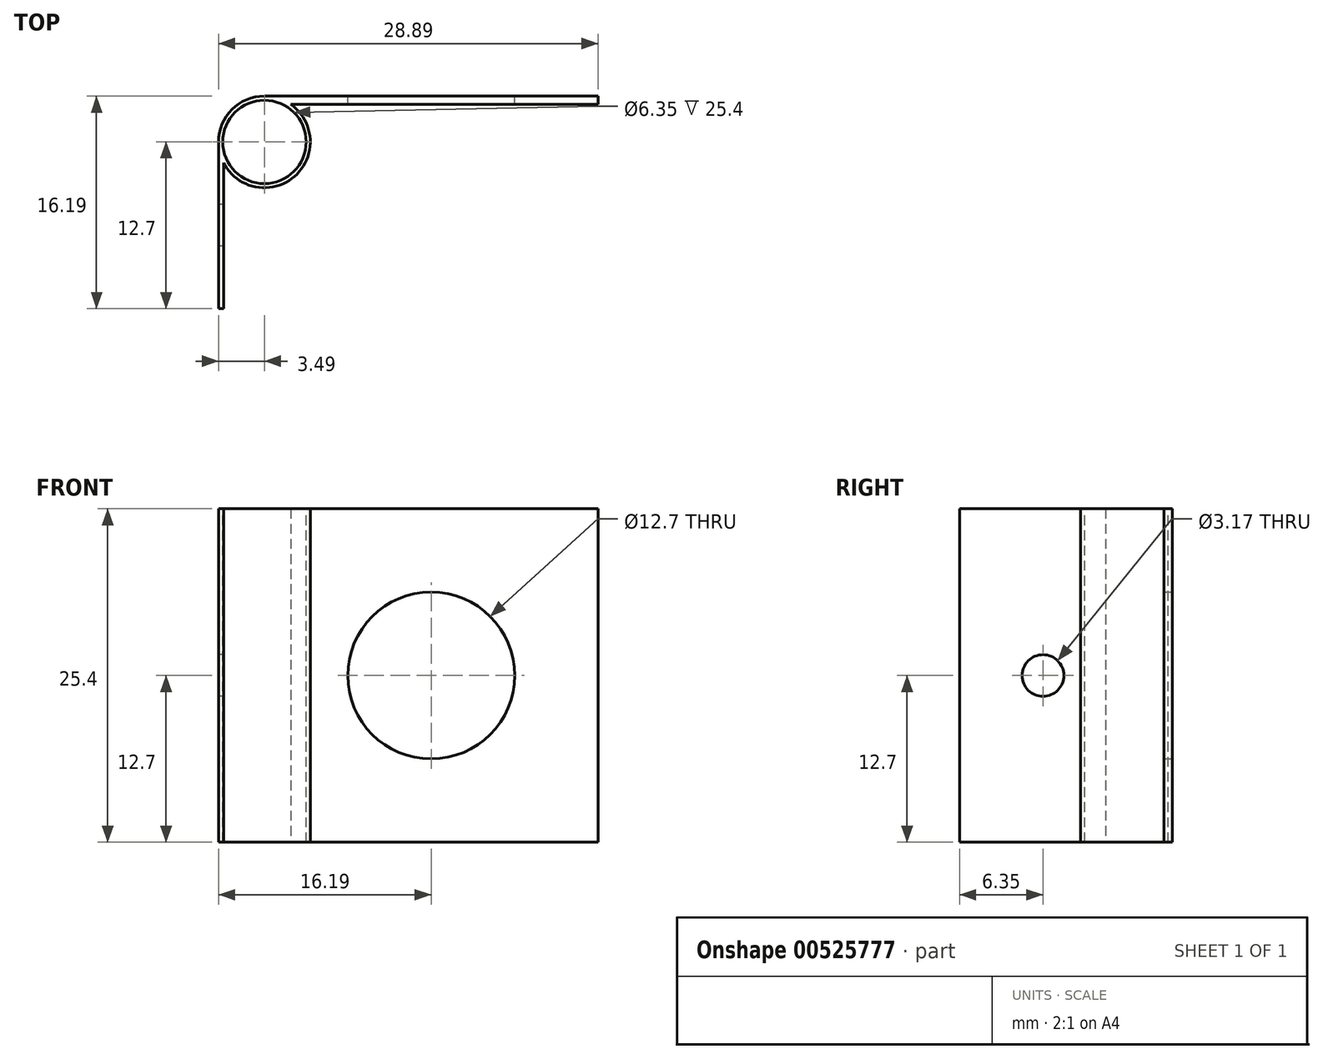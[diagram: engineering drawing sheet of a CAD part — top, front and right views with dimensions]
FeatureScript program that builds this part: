
annotation { "Feature Type Name" : "Feature", "Feature Type Description" : "" }
export const myFeature = defineFeature(function(context is Context, id is Id, definition is map)
    precondition{}
    {
        {
            var Q0;
            Q0=qCreatedBy(makeId("Top.planeOp"),FACE);
            var sketch = newSketch(context, id + "F0", { "sketchPlane" : qUnion([Q0])});
            skCircle(sketch, "E0", {"center": v(0, 0) * mm, "radius": 3.5 * mm});
            skLineSegment(sketch, "E1", {"start": v(0, 3.5) * mm, "end": v(25.4, 3.5) * mm});
            skLineSegment(sketch, "E2", {"start": v(-3.5, 0) * mm, "end": v(-3.5, -12.7) * mm});
            skLineSegment(sketch, "E3", {"start": v(-3.5, -12.7) * mm, "end": v(-3.11, -12.7) * mm});
            skLineSegment(sketch, "E4", {"start": v(-3.11, -12.7) * mm, "end": v(-3.11, -1.59) * mm});
            skLineSegment(sketch, "E5", {"start": v(25.4, 3.5) * mm, "end": v(25.4, 2.86) * mm});
            skLineSegment(sketch, "E6", {"start": v(25.4, 2.86) * mm, "end": v(2, 2.86) * mm});
            skSolve(sketch);
        }
        {
            var Q0;
            {var subQ0=sQuery(id+"F0.wireOp",EDGE,"E0");var subQ1=makeQuery(id+"F0.imprint","INTERSECT",VERTEX,{"derivedFrom":[subQ0,sQuery(id+"F0.wireOp",EDGE,"E1")]});Q0=makeQuery(id+"F0.imprint","IMPRINT",FACE,{"disambiguationData":[TD([[makeQuery(id+"F0.imprint","IMPRINT",EDGE,{"disambiguationData":[TD([[subQ1,1.0]])],"derivedFrom":subQ0}),1.0]])]});}
            var Q1;
            {var subQ0=sQuery(id+"F0.wireOp",EDGE,"E1");Q1=makeQuery(id+"F0.imprint","IMPRINT",FACE,{"disambiguationData":[TD([[makeQuery(id+"F0.imprint","IMPRINT",EDGE,{"derivedFrom":subQ0}),-1.0]])]});}
            var Q2;
            {var subQ0=sQuery(id+"F0.wireOp",EDGE,"E2");Q2=makeQuery(id+"F0.imprint","IMPRINT",FACE,{"disambiguationData":[TD([[makeQuery(id+"F0.imprint","IMPRINT",EDGE,{"derivedFrom":subQ0}),1.0]])]});}
            extrude(context, id + "F1", {"entities" : qUnion([Q0, Q1, Q2]), "depth" : 25.4 * mm, "offsetDistance" : 25.4 * mm});
        }
        {
            var Q0;
            Q0=makeQuery(id+"F1.opExtrude","SWEPT_FACE",FACE,{"disambiguationData":[OSD([sQuery(id+"F0.wireOp",EDGE,"E2")])]});
            var sketch = newSketch(context, id + "F2", { "sketchPlane" : qUnion([Q0])});
            skCircle(sketch, "E7", {"center": v(6.35, 12.7) * mm, "radius": 1.59 * mm});
            skSolve(sketch);
        }
        {
            var Q0;
            Q0=sQuery(id+"F2.wireOp",VERTEX,"E7.center");
            var Q1;
            Q1=makeQuery(id+"F1.opExtrude","SWEPT_BODY",BODY,{"disambiguationData":[OSD([sQuery(id+"F0.wireOp",EDGE,"E0"),sQuery(id+"F0.wireOp",EDGE,"E1"),sQuery(id+"F0.wireOp",EDGE,"E2"),sQuery(id+"F0.wireOp",EDGE,"E3"),sQuery(id+"F0.wireOp",EDGE,"E4"),sQuery(id+"F0.wireOp",EDGE,"E5"),sQuery(id+"F0.wireOp",EDGE,"E6")])]});
            hole(context, id + "F3", {"style" : HoleStyle.SIMPLE, "endStyle" : HoleEndStyle.THROUGH, "holeDiameter" : 3.17 * mm, "isTappedThrough" : true, "tappedDepth" : 12.7 * mm, "tapClearance" : 3, "locations" : qUnion([Q0]), "scope" : qUnion([Q1])});
        }
        {
            var Q0;
            Q0=makeQuery(id+"F1.opExtrude","SWEPT_FACE",FACE,{"disambiguationData":[OSD([sQuery(id+"F0.wireOp",EDGE,"E1")])]});
            var sketch = newSketch(context, id + "F4", { "sketchPlane" : qUnion([Q0])});
            skCircle(sketch, "E8", {"center": v(-12.7, 12.7) * mm, "radius": 6.35 * mm});
            skSolve(sketch);
        }
        {
            var Q0;
            Q0=sQuery(id+"F4.wireOp",VERTEX,"E8.center");
            var Q1;
            Q1=makeQuery(id+"F1.opExtrude","SWEPT_BODY",BODY,{"disambiguationData":[OSD([sQuery(id+"F0.wireOp",EDGE,"E0"),sQuery(id+"F0.wireOp",EDGE,"E1"),sQuery(id+"F0.wireOp",EDGE,"E2"),sQuery(id+"F0.wireOp",EDGE,"E3"),sQuery(id+"F0.wireOp",EDGE,"E4"),sQuery(id+"F0.wireOp",EDGE,"E5"),sQuery(id+"F0.wireOp",EDGE,"E6")])]});
            hole(context, id + "F5", {"style" : HoleStyle.SIMPLE, "endStyle" : HoleEndStyle.THROUGH, "holeDiameter" : 12.7 * mm, "isTappedThrough" : true, "tappedDepth" : 12.7 * mm, "tapClearance" : 3, "locations" : qUnion([Q0]), "scope" : qUnion([Q1])});
        }
        {
            var Q0;
            Q0=makeQuery(id+"F1.opExtrude","CAP_FACE",FACE,{"disambiguationData":[OSD([sQuery(id+"F0.wireOp",EDGE,"E0"),sQuery(id+"F0.wireOp",EDGE,"E1"),sQuery(id+"F0.wireOp",EDGE,"E2"),sQuery(id+"F0.wireOp",EDGE,"E3"),sQuery(id+"F0.wireOp",EDGE,"E4"),sQuery(id+"F0.wireOp",EDGE,"E5"),sQuery(id+"F0.wireOp",EDGE,"E6")])],"isStart":false});
            var sketch = newSketch(context, id + "F6", { "sketchPlane" : qUnion([Q0])});
            skCircle(sketch, "E9", {"center": v(0, 0) * mm, "radius": 0.94 * mm});
            skSolve(sketch);
        }
        {
            var Q0;
            Q0=sQuery(id+"F6.wireOp",VERTEX,"E9.center");
            var Q1;
            Q1=makeQuery(id+"F1.opExtrude","SWEPT_BODY",BODY,{"disambiguationData":[OSD([sQuery(id+"F0.wireOp",EDGE,"E0"),sQuery(id+"F0.wireOp",EDGE,"E1"),sQuery(id+"F0.wireOp",EDGE,"E2"),sQuery(id+"F0.wireOp",EDGE,"E3"),sQuery(id+"F0.wireOp",EDGE,"E4"),sQuery(id+"F0.wireOp",EDGE,"E5"),sQuery(id+"F0.wireOp",EDGE,"E6")])]});
            hole(context, id + "F7", {"style" : HoleStyle.SIMPLE, "endStyle" : HoleEndStyle.THROUGH, "holeDiameter" : 6.35 * mm, "isTappedThrough" : true, "tappedDepth" : 12.7 * mm, "tapClearance" : 3, "locations" : qUnion([Q0]), "scope" : qUnion([Q1])});
        }
    });
